# Revit family: ledspotrs-p_35w-4000-60d-wh_541003068300
name_source: partatom
category: Leuchten
revit_build: Autodesk Revit 2016 (Build: 20190508_0715(x64)
units: mm (PartAtom-declared; Revit-internal decimal feet)

## family parameters
Basisbauteil = Fläche
Beim Laden mit Abzugskörper schneiden = Nein
Bemaßung runder Anschluss = Durchmesser verwenden
Gemeinsam genutzt = Nein
Lichtquelle = Nein
Raumberechnungspunkt = Nein
Teiletyp = Normal

## types (1)
- LEDSpotRS-P 35W-4000-60D-WH (1 x LED, 3500 lm)
    Approval mark = CE, ENEC
    Beschreibung = Powerful recessed, rotatable and tiltable spot. Clean and compact design ideal for retail shops, showrooms, and hospitality environments. Die-cast aluminium housing. Excellent colour rendering with CRI 90.
    CIE Flux Codes = 84 98 100 99 100
    Control Gear = Electronic ballast
    Height = 0 mm  [stored 0 ft]
    Hersteller = OPPLE
    Lamp Light Flux = 3500 lm
    Lamp count = 1
    Lampe = 1 x LED
    Length = 180 mm  [stored 0.590551 ft]
    Luminous efficacy = 100 lm/W
    ModVariant = Nein
    Modell = 541003068300
    Mounting Place = Ceiling
    Mounting Type = Recessed
    Number of Poles = 1
    OnlyDefault = Ja
    Power Factor = 1
    Product Name = LEDSpotRS-P 35W-4000-60D-WH
    Product group = Spot Performer Swing
    ProductGroupID = 423
    Protection Class = Protection class II
    Protection Degree = IP 20
    RLX_Detail_Level = 1
    RlxData = <blob elided: 166253 chars, md5=c3044fca>
    Scheinlast = 35 VA
    Socket = socket
    Standby Power = 0 W
    System Light Flux = 3500 lm
    System Power = 35 W
    Typenbild = 541003068300.jpg
    Typenkommentare = Product without accessories
    URL = http://relux.com
    VarID = ---
    Voltage = 0 V
    Vorgabe-Ansicht = 1800 mm
    Weight = 0.00 kg
    Width = 0 mm  [stored 0 ft]

note: [stored X ft] marks values corroborated as IEEE doubles in the binary element streams (Revit-internal decimal feet)

## geometry (parser evidence)
native form markers: Blend x4, Sweep x14
no freeform markers — native parametric forms only
